# Revit family: Sink_Kitchen-Fire_Clay-DXV-Orchard-D20100000
name_source: partatom
category: Plumbing Fixtures
revit_build: Autodesk Revit 2014 (Build: 20130308_1515(x64)
units: mm (PartAtom-declared; Revit-internal decimal feet)

## types (1)
- D20100000.415
    Assembly Code = D2010310
    Basin Shape = Rectangle
    CW Connection = Yes
    CWFU = 1.5
    Cold Water Connection Diameter = 1/2"
    Cold Water Connection Height = 22 3/4"
    Cold Water Connection Radius = 1/4"
    Cold Water Connection Width = 4"
    Default Elevation = 34"
    Description = Apron Front Kitchen Sink Canvas White
    HW Connection = Yes
    HWFU = 1.5
    Height = 10"
    Hot Water Connection Diameter = 1/2"
    Hot Water Connection Height = 22 3/4"
    Hot Water Connection Radius = 1/4"
    Hot Water Connection Width = 4"
    Installation Type = Semi Counter Mounted
    Length = 18"
    Manufacturer = DXV
    Material = Fire Clay-DXV-415-Canvas White
    Model = D20100000.415
    Price = Prices may vary. Please consult Manufacturer Representative for most up-to-date price list.
    Product Documentation Link = http://dxv.blob.core.windows.net
    Product Page URL = http://www.dxv.com
    Type Comments = Bottom sink rack and strainer included, commercial grade drain included
    URL = www.dxv.com
    Vent Connection = No
    WFU = 2
    Waste Connection = Yes
    Waste Connection Diameter = 1 1/4"
    Waste Connection Height = 20 1/4"
    Waste Connection Radius = 5/8"
    Width = 20"

## geometry (parser evidence)
native form markers: Sweep x1
no freeform markers — native parametric forms only
